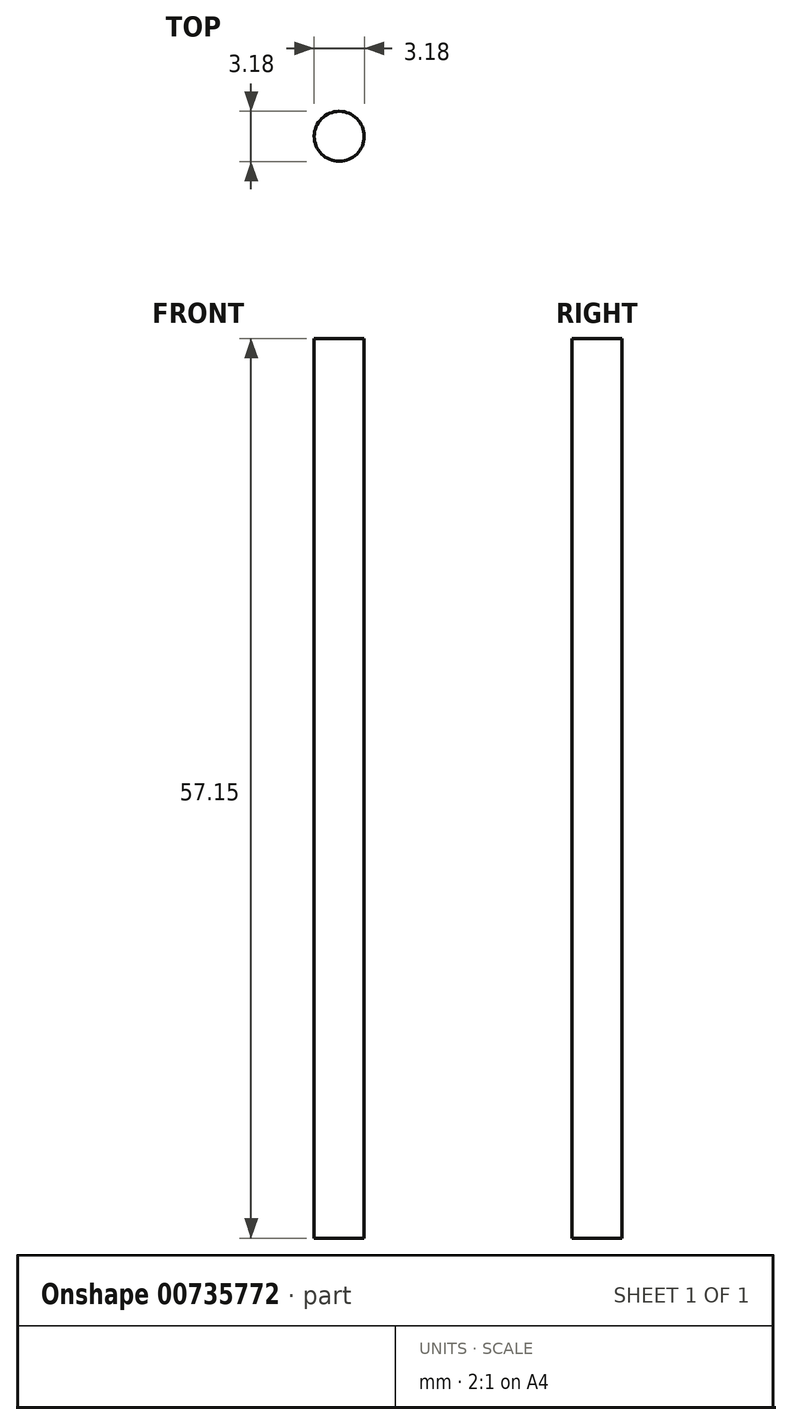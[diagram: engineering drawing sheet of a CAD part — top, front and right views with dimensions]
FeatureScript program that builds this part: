
annotation { "Feature Type Name" : "Feature", "Feature Type Description" : "" }
export const myFeature = defineFeature(function(context is Context, id is Id, definition is map)
    precondition{}
    {
        {
            var Q0;
            Q0=qCreatedBy(makeId("Top.planeOp"),FACE);
            var sketch = newSketch(context, id + "F0", { "sketchPlane" : qUnion([Q0])});
            skCircle(sketch, "E0", {"center": v(0, 0) * mm, "radius": 1.59 * mm});
            skSolve(sketch);
        }
        {
            var Q0;
            Q0 = qSketchRegion(id + "F0", true);
            extrude(context, id + "F1", {"entities" : qUnion([Q0]), "depth" : 57.15 * mm, "offsetDistance" : 25.4 * mm});
        }
    });
